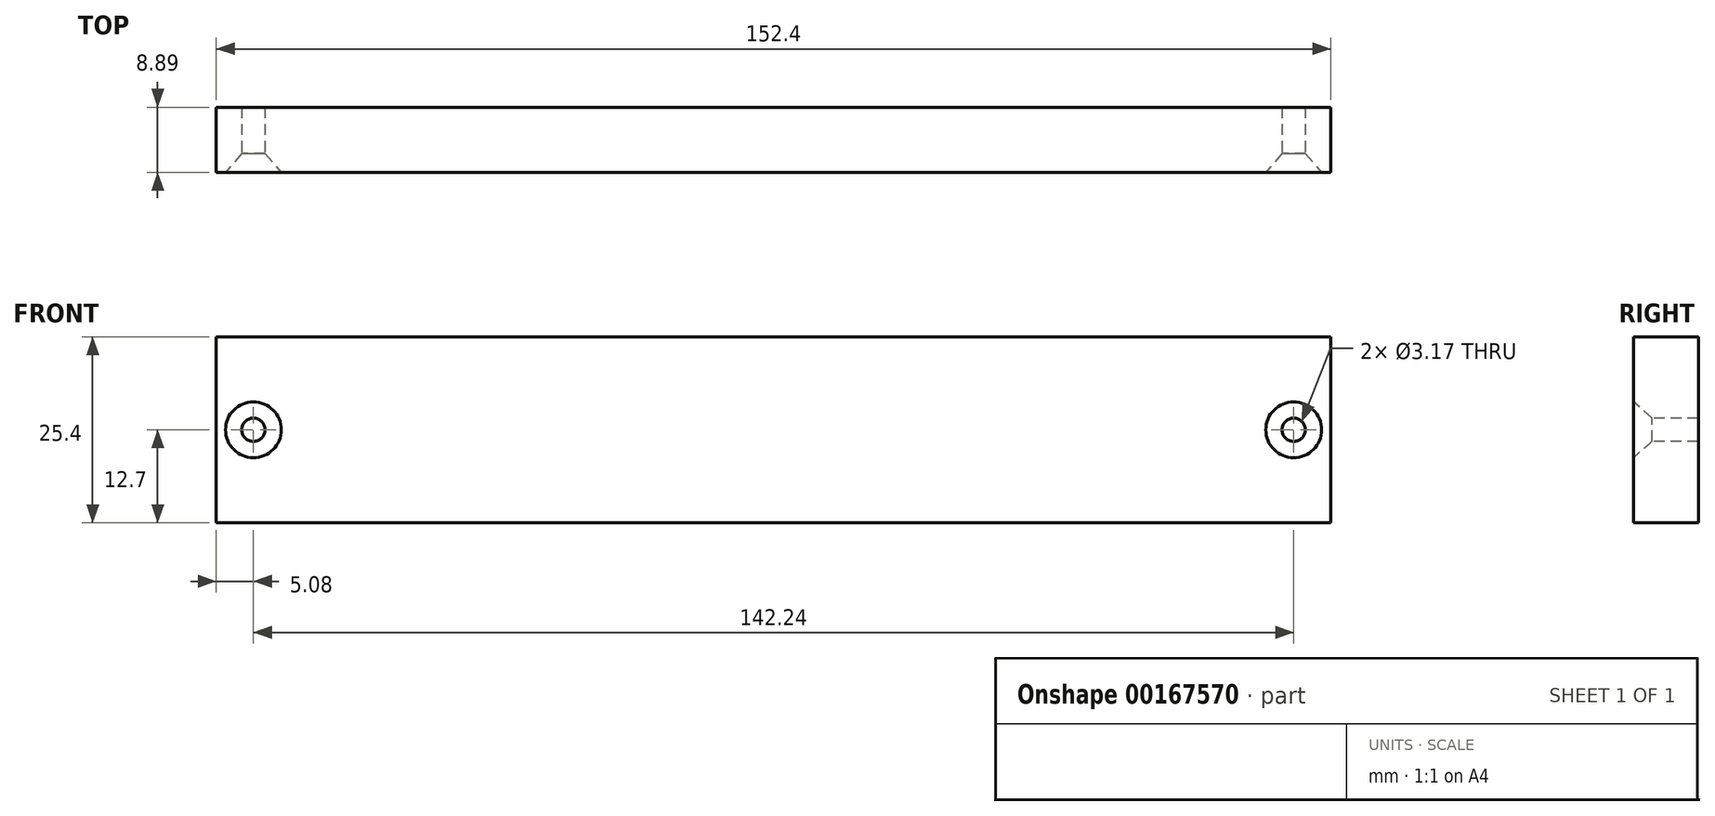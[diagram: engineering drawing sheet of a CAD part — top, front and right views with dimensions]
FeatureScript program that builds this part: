
annotation { "Feature Type Name" : "Feature", "Feature Type Description" : "" }
export const myFeature = defineFeature(function(context is Context, id is Id, definition is map)
    precondition{}
    {
        {
            var Q0;
            Q0=qCreatedBy(makeId("Front.planeOp"),FACE);
            var sketch = newSketch(context, id + "F0", { "sketchPlane" : qUnion([Q0])});
            skLineSegment(sketch, "E0.bottom", {"start": v(0, 0) * mm, "end": v(152.4, 0) * mm});
            skLineSegment(sketch, "E0.top", {"start": v(0, 25.4) * mm, "end": v(152.4, 25.4) * mm});
            skLineSegment(sketch, "E0.left", {"start": v(0, 0) * mm, "end": v(0, 25.4) * mm});
            skLineSegment(sketch, "E0.right", {"start": v(152.4, 0) * mm, "end": v(152.4, 25.4) * mm});
            skSolve(sketch);
        }
        {
            var Q0;
            Q0 = qSketchRegion(id + "F0", true);
            extrude(context, id + "F1", {"entities" : qUnion([Q0]), "depth" : 8.9 * mm});
        }
        {
            var Q0;
            Q0=makeQuery(id+"F1.opExtrude","CAP_FACE",FACE,{"disambiguationData":[OSD([sQuery(id+"F0.wireOp",EDGE,"E0.bottom"),sQuery(id+"F0.wireOp",EDGE,"E0.top"),sQuery(id+"F0.wireOp",EDGE,"E0.left"),sQuery(id+"F0.wireOp",EDGE,"E0.right")])],"isStart":false});
            var sketch = newSketch(context, id + "F2", { "sketchPlane" : qUnion([Q0])});
            skPoint(sketch, "E1", {"position": v(5.08, 12.7) * mm});
            skPoint(sketch, "E1.positionSnap0", {"position": v(0, 12.7) * mm});
            skPoint(sketch, "E2", {"position": v(152.4, 12.7) * mm});
            skPoint(sketch, "E3", {"position": v(147.32, 12.7) * mm});
            skSolve(sketch);
        }
        {
            var Q0;
            Q0=sQuery(id+"F2.wireOp",VERTEX,"E1");
            var Q1;
            Q1=sQuery(id+"F2.wireOp",VERTEX,"E3");
            var Q2;
            Q2=makeQuery(id+"F1.opExtrude","SWEPT_BODY",BODY,{"disambiguationData":[OSD([sQuery(id+"F0.wireOp",EDGE,"E0.bottom"),sQuery(id+"F0.wireOp",EDGE,"E0.top"),sQuery(id+"F0.wireOp",EDGE,"E0.left"),sQuery(id+"F0.wireOp",EDGE,"E0.right")])]});
            hole(context, id + "F3", {"style" : HoleStyle.C_SINK, "endStyle" : HoleEndStyle.THROUGH, "holeDiameter" : 3.17 * mm, "cSinkDiameter" : 7.62 * mm, "cSinkAngle" : 82 * degree, "locations" : qUnion([Q0, Q1]), "scope" : qUnion([Q2]), "isTappedThrough" : true});
        }
    });
